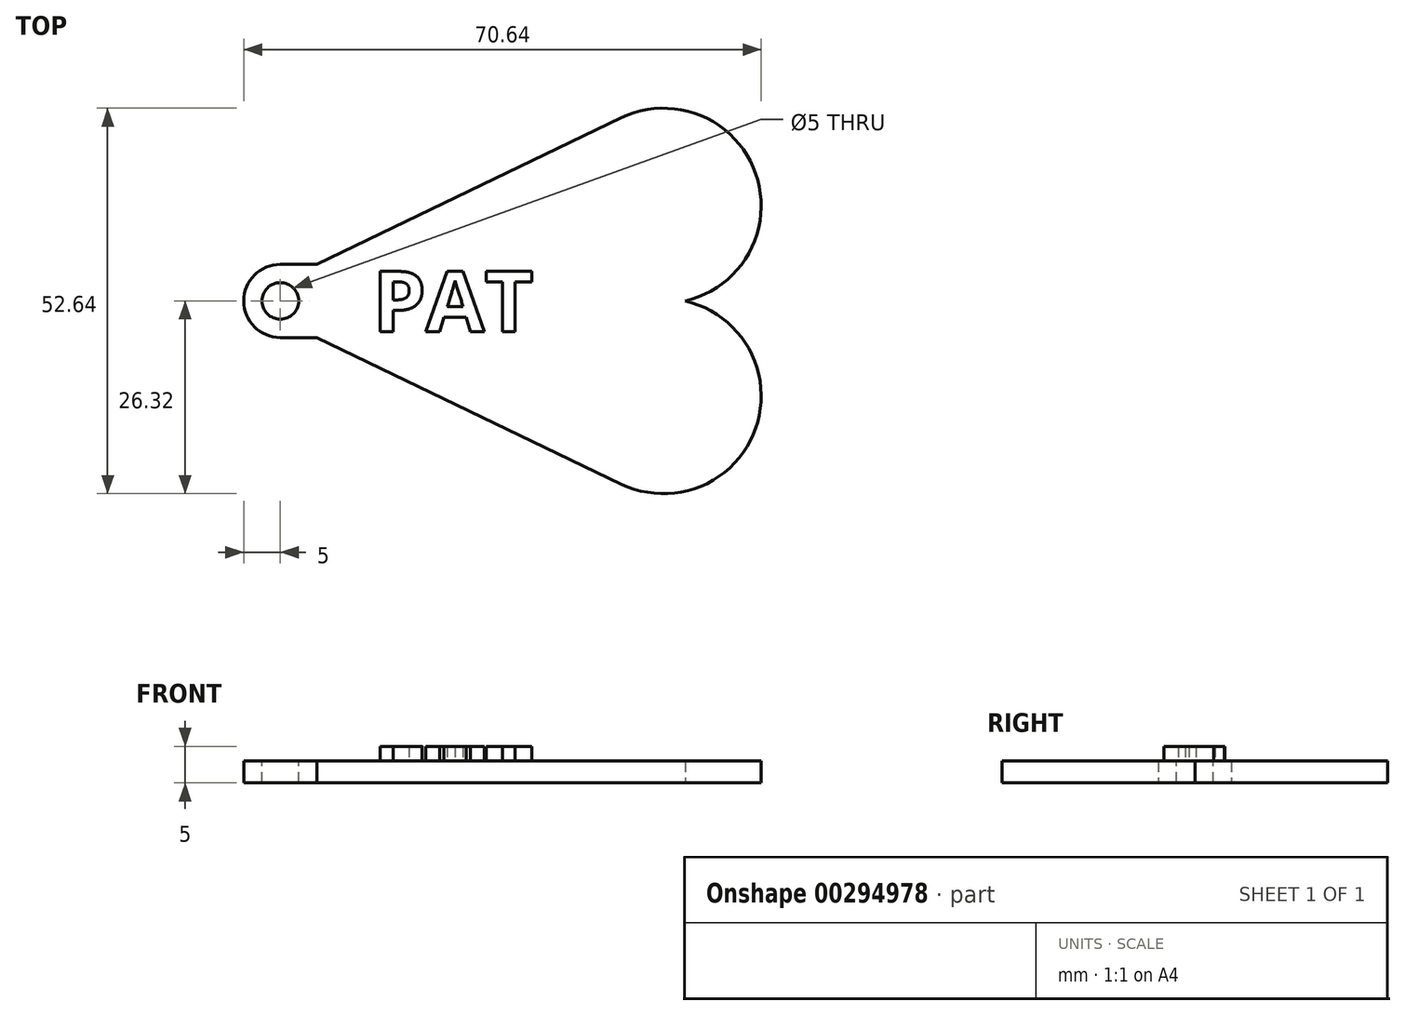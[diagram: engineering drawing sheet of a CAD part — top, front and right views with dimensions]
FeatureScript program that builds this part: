
annotation { "Feature Type Name" : "Feature", "Feature Type Description" : "" }
export const myFeature = defineFeature(function(context is Context, id is Id, definition is map)
    precondition{}
    {
        {
            var Q0;
            Q0=qCreatedBy(makeId("Top.planeOp"),FACE);
            var sketch = newSketch(context, id + "F0", { "sketchPlane" : qUnion([Q0])});
            skPoint(sketch, "E0.middle", {"position": v(0, 0) * mm});
            skLineSegment(sketch, "E1.bottom", {"start": v(-32.5, 5) * mm, "end": v(-37.5, 5) * mm});
            skLineSegment(sketch, "E1.top", {"start": v(-32.5, -5) * mm, "end": v(-37.5, -5) * mm});
            skLineSegment(sketch, "E1.right", {"start": v(-42.5, 0) * mm, "end": v(-42.5, 0) * mm});
            skPoint(sketch, "E2.visualSharp", {"position": v(-42.5, 5) * mm});
            skArc(sketch, "E2.filletArc", {"start": v(-37.5, 5) * mm, "mid": v(-41.04, 3.54) * mm, "end": v(-42.5, 0) * mm});
            skPoint(sketch, "E3.visualSharp", {"position": v(-42.5, -5) * mm});
            skArc(sketch, "E3.filletArc", {"start": v(-42.5, 0) * mm, "mid": v(-41.04, -3.54) * mm, "end": v(-37.5, -5) * mm});
            skLineSegment(sketch, "E4", {"start": v(-32.5, 5) * mm, "end": v(9.04, 25) * mm});
            skArc(sketch, "E5", {"start": v(17.76, 0) * mm, "mid": v(27.4, 17.39) * mm, "end": v(9.04, 25) * mm});
            skLineSegment(sketch, "E6.MirrorCS", {"start": v(-32.5, -5) * mm, "end": v(9.04, -25) * mm});
            skArc(sketch, "E7.MirrorCS", {"start": v(17.76, 0) * mm, "mid": v(27.4, -17.39) * mm, "end": v(9.04, -25) * mm});
            skSolve(sketch);
        }
        {
            var Q0;
            Q0=makeQuery(id+"F0.imprint","IMPRINT",FACE,{"disambiguationData":[TD([[makeQuery(id+"F0.imprint","IMPRINT",EDGE,{"derivedFrom":sQuery(id+"F0.wireOp",EDGE,"E1.bottom")}),1.0]])]});
            extrude(context, id + "F1", {"entities" : qUnion([Q0]), "depth" : 3 * mm});
        }
        {
            var Q0;
            Q0=makeQuery(id+"F1.opExtrude","CAP_FACE",FACE,{"disambiguationData":[OSD([sQuery(id+"F0.wireOp",EDGE,"E0.bottom"),sQuery(id+"F0.wireOp",EDGE,"E0.top"),sQuery(id+"F0.wireOp",EDGE,"E0.left"),sQuery(id+"F0.wireOp",EDGE,"E0.right"),sQuery(id+"F0.wireOp",EDGE,"E1.bottom"),sQuery(id+"F0.wireOp",EDGE,"E1.top"),sQuery(id+"F0.wireOp",EDGE,"1765a43f-fdfe-47e4-afa1-6d42d2fb76db.trimOffspring"),sQuery(id+"F0.wireOp",EDGE,"E2.filletArc"),sQuery(id+"F0.wireOp",EDGE,"E3.filletArc"),sQuery(id+"F0.wireOp",EDGE,"4ba67fea-818f-4445-a108-3683f4bda5c0.filletArc"),sQuery(id+"F0.wireOp",EDGE,"3327f9a1-dff7-428a-b146-fdb06a1d8770.filletArc"),sQuery(id+"F0.wireOp",EDGE,"8cacc379-9569-44a9-b1fd-9f137b584586.filletArc"),sQuery(id+"F0.wireOp",EDGE,"2aa8920c-0d52-40b2-9e8e-5a556ab7ae1f.filletArc")])],"isStart":false});
            var sketch = newSketch(context, id + "F2", { "sketchPlane" : qUnion([Q0])});
            skCircle(sketch, "E8", {"center": v(-37.5, 0) * mm, "radius": 2.5 * mm});
            skSolve(sketch);
        }
        {
            var Q0;
            Q0=makeQuery(id+"F2.imprint","IMPRINT",FACE,{"disambiguationData":[TD([[makeQuery(id+"F2.imprint","IMPRINT",EDGE,{"derivedFrom":sQuery(id+"F2.wireOp",EDGE,"E8")}),1.0]])]});
            extrude(context, id + "F3", {"entities" : qUnion([Q0]), "operationType" : NewBodyOperationType.REMOVE, "endBound" : BoundingType.UP_TO_NEXT, "oppositeDirection" : true, "depth" : 25 * mm});
        }
        {
            var Q0;
            Q0=makeQuery(id+"F1.opExtrude","CAP_FACE",FACE,{"disambiguationData":[OSD([sQuery(id+"F0.wireOp",EDGE,"E0.bottom"),sQuery(id+"F0.wireOp",EDGE,"E0.top"),sQuery(id+"F0.wireOp",EDGE,"E0.left"),sQuery(id+"F0.wireOp",EDGE,"E0.right"),sQuery(id+"F0.wireOp",EDGE,"E1.bottom"),sQuery(id+"F0.wireOp",EDGE,"E1.top"),sQuery(id+"F0.wireOp",EDGE,"1765a43f-fdfe-47e4-afa1-6d42d2fb76db.trimOffspring"),sQuery(id+"F0.wireOp",EDGE,"E2.filletArc"),sQuery(id+"F0.wireOp",EDGE,"E3.filletArc"),sQuery(id+"F0.wireOp",EDGE,"4ba67fea-818f-4445-a108-3683f4bda5c0.filletArc"),sQuery(id+"F0.wireOp",EDGE,"3327f9a1-dff7-428a-b146-fdb06a1d8770.filletArc"),sQuery(id+"F0.wireOp",EDGE,"8cacc379-9569-44a9-b1fd-9f137b584586.filletArc"),sQuery(id+"F0.wireOp",EDGE,"2aa8920c-0d52-40b2-9e8e-5a556ab7ae1f.filletArc")])],"isStart":false});
            var sketch = newSketch(context, id + "F4", { "sketchPlane" : qUnion([Q0])});
            skText(sketch, "E9", { "text": "PAT", "fontName": "OpenSans-Bold.ttf"});
            skPoint(sketch, "E10", {"position": v(-35, 5) * mm});
            const initialGuessF4  = {"E9": [-0.02488, -0.00422, 1, 0, 0.00832]};
            skSetInitialGuess(sketch, initialGuessF4);
            skSolve(sketch);
        }
        {
            var Q0;
            Q0=makeQuery(id+"F4.imprint","IMPRINT",FACE,{"disambiguationData":[TD([[makeQuery(id+"F4.imprint","IMPRINT",EDGE,{"derivedFrom":sQuery(id+"F4.wireOp",EDGE,"E9.sketch_text.stroke-0")}),-1.0]])]});
            var Q1;
            Q1=makeQuery(id+"F4.imprint","IMPRINT",FACE,{"disambiguationData":[TD([[makeQuery(id+"F4.imprint","IMPRINT",EDGE,{"derivedFrom":sQuery(id+"F4.wireOp",EDGE,"E9.sketch_text.stroke-10")}),-1.0]])]});
            var Q2;
            Q2=makeQuery(id+"F4.imprint","IMPRINT",FACE,{"disambiguationData":[TD([[makeQuery(id+"F4.imprint","IMPRINT",EDGE,{"derivedFrom":sQuery(id+"F4.wireOp",EDGE,"E9.sketch_text.stroke-29")}),-1.0]])]});
            var Q3;
            Q3=makeQuery(id+"F4.imprint","IMPRINT",FACE,{"disambiguationData":[TD([[makeQuery(id+"F4.imprint","IMPRINT",EDGE,{"derivedFrom":sQuery(id+"F4.wireOp",EDGE,"E9.sketch_text.stroke-41")}),-1.0]])]});
            var Q4;
            Q4=makeQuery(id+"F4.imprint","IMPRINT",FACE,{"disambiguationData":[TD([[makeQuery(id+"F4.imprint","IMPRINT",EDGE,{"derivedFrom":sQuery(id+"F4.wireOp",EDGE,"E9.sketch_text.stroke-50")}),-1.0]])]});
            var Q5;
            Q5=makeQuery(id+"F4.imprint","IMPRINT",FACE,{"disambiguationData":[TD([[makeQuery(id+"F4.imprint","IMPRINT",EDGE,{"derivedFrom":sQuery(id+"F4.wireOp",EDGE,"E9.sketch_text.stroke-16")}),-1.0]])]});
            extrude(context, id + "F5", {"entities" : qUnion([Q0, Q1, Q2, Q3, Q4, Q5]), "operationType" : NewBodyOperationType.ADD, "depth" : 2 * mm});
        }
    });
